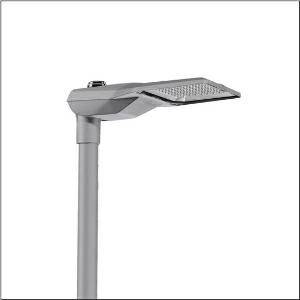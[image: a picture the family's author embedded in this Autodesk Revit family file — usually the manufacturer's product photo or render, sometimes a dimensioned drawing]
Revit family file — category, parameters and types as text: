
# Revit family: streetlight_sl_21_midi___st0_5a_5xe7b47n08lb_dab4
name_source: partatom
category: Lighting Fixtures
units: mm (PartAtom-declared; Revit-internal decimal feet)

## family parameters
Cut with Voids When Loaded = No
Host = Face
Light Source = No
Part Type = Normal
Room Calculation Point = No
Round Connector Dimension = Use Diameter
Shared = No

## types (1)
- --- (1 x LED, 14950 lm, 98.3 W, 4000K)
    Apparent Load = 98 VA
    CIE Flux Codes = 41 75 97 100 100
    Color Rendering = 70
    Color Temperature = 4000K
    Default Elevation = 1800 mm
    Description = Streetlight SL 21 midi, mast luminaire, primary light control with lens, of PMMA, primary optical cover: cover, of toughened safety glass, transparent, light distribution: ST0.5a, light emission: direct distribution, primary light characteristic: asymmetric, installation type: side-entry, LED, 3G 2.5mm², High Power LED, rated luminous flux: 14.950lm, luminous efficacy: 152lm/W, light colour: 740, colour temperature: 4000K, control gear: NEMA (7pin), control: overheat protection, pre-setting: linear dimming characteristic, constant luminous flux control, time-dependent luminous flux control, flexible luminous flux parameterisation, mains connection: 220..240V, AC, 50/60Hz, connection cable pre-assembled, cable length: 10,5m, wiring characteristics: H05VV-F, start of lifetime: 98W, end of service life: 101W, reduction: 45W, luminaire housing, of diecast aluminium (EN AC-44300), powder-coated, SITECO metallic grey (DB 702S), corrosivity category C5 high according to DIN EN ISO 12944, multi-level sealing system, sealing non-destructively replaceable, inclination adjustable: 0°, 5°, 10°, 15°, length: 644mm, width: 335mm, height: 110mm, spigot size: 42mm (side-entry), mounting height: 4..8m, protection rating (complete): IP66, insulation class (complete): insulation class I (protective earthing), certification: CE, ENEC, ENEC+, VDE, impact resistance: IK10, permissible operating ambient temperature for outdoor applications: -40..+50°C, standard-compliant lighting for roads and squares, packaging unit: 1 piece

Light Distribution: ST0.5a
    Height = 111 mm
    Lamp = 1 x LED
    Lamp Light Flux = 14950 lm
    Lamp Power = 98.3 W
    Lamp count = 1
    Length = 644 mm
    Luminous efficacy = 152 lm/W
    Manufacturer = Siteco
    ModVariant = No
    Model = 5XE7B47N08LB
    Mounting Place = Pole
    Mounting Type = Pole top
    Number of Poles = 1
    OnlyDefault = Yes
    Power Factor = 1
    Product Name = Streetlight SL 21 midi | ST0.5a
    Product group = mast luminaire | pylon top
    ProductGroupID = 6100
    Protection Class = Protection class I
    Protection Degree = IP 66
    RLX_Detail_Level = 1
    RLX_Emergency_Light_Flux = 0 lm
    RLX_Emergency_Type = 0
    RLX_Emergency_Type_DB = No
    RlxData = <blob elided: 37765 chars, md5=2dd48341>
    Socket = socket
    Standby Power = 0 W
    System Light Flux = 14950 lm
    System Power = 98 W
    Type Comments = factory setting: luminous flux: 100 % | dim-lin: 254 | 1020 mA
    Type Image = l_1294377.jpg
    URL = http://relux.com
    VarID = @adj_138351
    Voltage = 0 V
    Weight = 0.00 kg
    Width = 336 mm

## geometry (parser evidence)
native form markers: Blend x4, Sweep x12
no freeform markers — native parametric forms only
